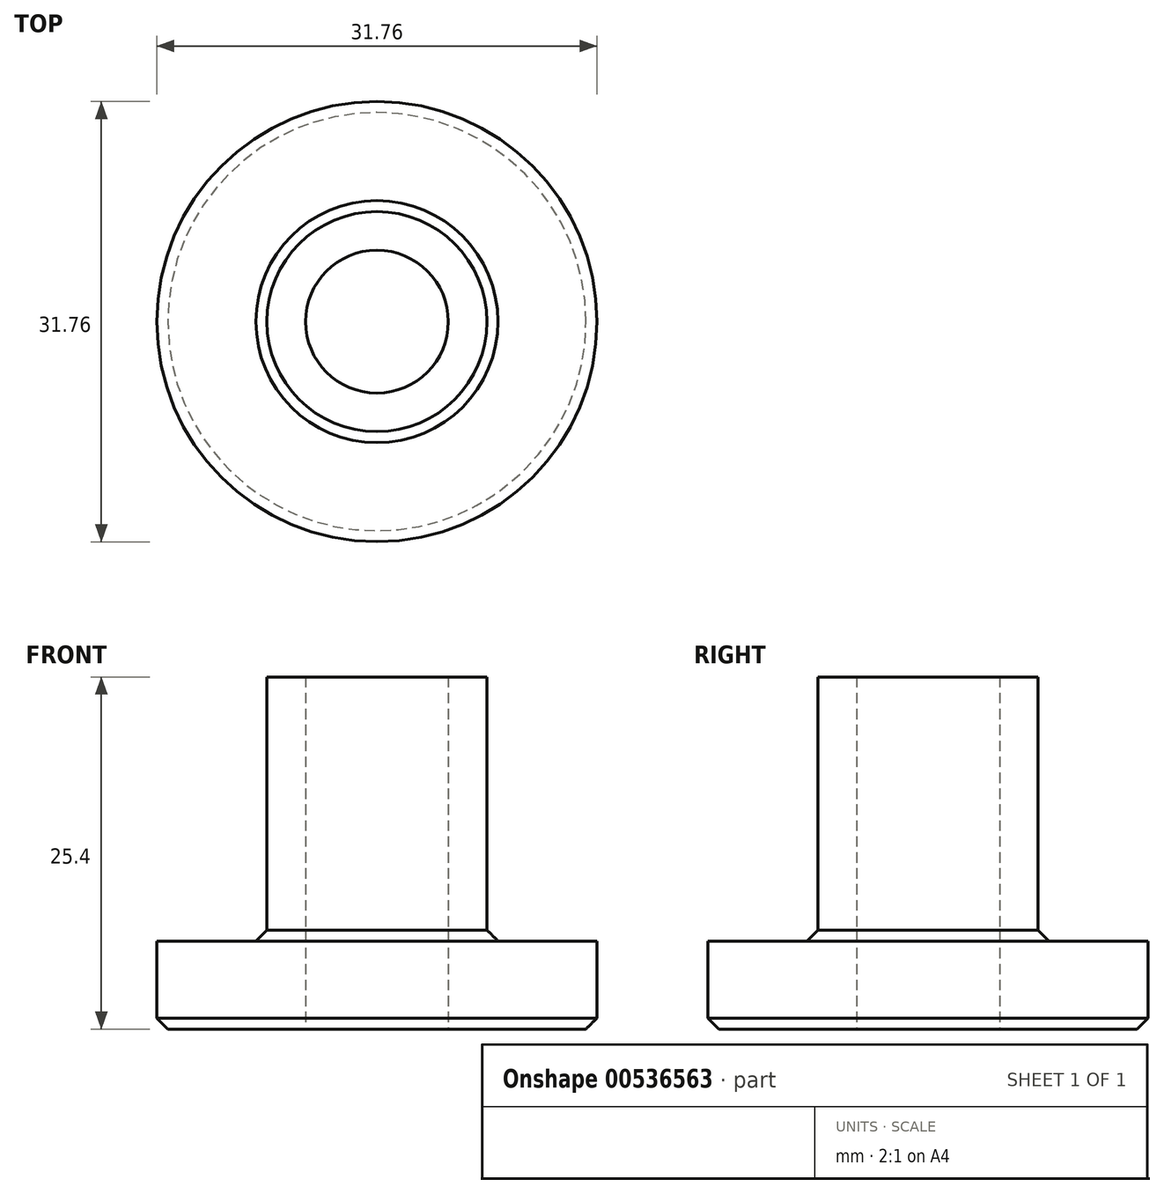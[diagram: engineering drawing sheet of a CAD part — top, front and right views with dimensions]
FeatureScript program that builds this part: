
annotation { "Feature Type Name" : "Feature", "Feature Type Description" : "" }
export const myFeature = defineFeature(function(context is Context, id is Id, definition is map)
    precondition{}
    {
        {
            var Q0;
            Q0=qCreatedBy(makeId("Top.planeOp"),FACE);
            var sketch = newSketch(context, id + "F0", { "sketchPlane" : qUnion([Q0])});
            skCircle(sketch, "E0", {"center": v(0, 0) * mm, "radius": 15.88 * mm});
            skSolve(sketch);
        }
        {
            var Q0;
            Q0=qSketchRegion(id+"F0",true);
            extrude(context, id + "F1", {"entities" : qUnion([Q0]), "depth" : 25.4 * mm, "offsetDistance" : 25.4 * mm});
        }
        {
            var Q0;
            Q0=sQuery(id+"F0.wireOp",VERTEX,"E0.center");
            var Q1;
            Q1=makeQuery(id+"F1.opExtrude","SWEPT_BODY",BODY,{"disambiguationData":[OSD([sQuery(id+"F0.wireOp",EDGE,"E0")])]});
            hole(context, id + "F2", {"style" : HoleStyle.SIMPLE, "endStyle" : HoleEndStyle.THROUGH, "oppositeDirection" : true, "standardTappedOrClearance" : lookupTablePath({ "standard" : "ISO", "engagement" : "75%", "pitch" : "1.75 mm", "size" : "M12", "type" : "Tapped" }), "standardBlindInLast" : lookupTablePath({ "standard" : "ISO", "engagement" : "75%", "pitch" : "1.75 mm", "size" : "M12", "type" : "Tapped" }), "holeDiameter" : 10.3 * mm, "showTappedDepth" : true, "isTappedThrough" : true, "tappedDepth" : 15.88 * mm, "tapClearance" : 3, "startFromSketch" : true, "locations" : qUnion([Q0]), "scope" : qUnion([Q1]), "majorDiameter" : 12 * mm});
        }
        {
            var Q0;
            Q0=makeQuery(id+"F1.opExtrude","CAP_EDGE",EDGE,{"disambiguationData":[OSD([sQuery(id+"F0.wireOp",EDGE,"E0")])],"isStart":true});
            chamfer(context, id + "F3", {"entities" : qUnion([Q0]), "width" : 0.8 * mm, "tangentPropagation" : true});
        }
        {
            var Q0;
            Q0=makeQuery(id+"F1.opExtrude","CAP_EDGE",EDGE,{"disambiguationData":[OSD([sQuery(id+"F0.wireOp",EDGE,"E0")])],"isStart":false});
            var Q1;
            Q1=makeQuery(id+"F2.hole-0.boolean.opBoolean","COPY",EDGE,{"derivedFrom":makeQuery(id+"F2.hole-0.opRevolve","SWEPT_EDGE",EDGE,{"disambiguationData":[OSD([sQuery(id+"F2.hole-0.sketch.wireOp",EDGE,"core_line_2"),sQuery(id+"F2.hole-0.sketch.wireOp",EDGE,"core_line_3")])]})});
            var Q2;
            Q2=makeQuery(id+"F2.hole-0.boolean.opBoolean","INTERSECT",EDGE,{"derivedFrom":[makeQuery(id+"F1.opExtrude","CAP_FACE",FACE,{"disambiguationData":[OSD([sQuery(id+"F0.wireOp",EDGE,"E0")])],"isStart":false}),makeQuery(id+"F2.hole-0.opRevolve","SWEPT_FACE",FACE,{"disambiguationData":[OSD([sQuery(id+"F2.hole-0.sketch.wireOp",EDGE,"core_line_2")])]})]});
            chamfer(context, id + "F4", {"entities" : qUnion([Q0, Q1, Q2]), "width" : 0.8 * mm, "tangentPropagation" : true});
        }
        {
            var Q0;
            Q0=makeQuery(id+"F1.opExtrude","CAP_FACE",FACE,{"disambiguationData":[OSD([sQuery(id+"F0.wireOp",EDGE,"E0")])],"isStart":false});
            var sketch = newSketch(context, id + "F5", { "sketchPlane" : qUnion([Q0])});
            skCircle(sketch, "E1", {"center": v(0, 0) * mm, "radius": 7.94 * mm});
            skCircle(sketch, "E2", {"center": v(0, 0) * mm, "radius": 15.88 * mm});
            skSolve(sketch);
        }
        {
            var Q0;
            Q0=qSketchRegion(id+"F5",true);
            extrude(context, id + "F6", {"entities" : qUnion([Q0]), "operationType" : NewBodyOperationType.REMOVE, "oppositeDirection" : true, "depth" : 19.05 * mm, "offsetDistance" : 25.4 * mm});
        }
        {
            var Q0;
            Q0=makeQuery(id+"F6.boolean.opBoolean","COPY",EDGE,{"derivedFrom":makeQuery(id+"F6.opExtrude","CAP_EDGE",EDGE,{"disambiguationData":[OSD([sQuery(id+"F5.wireOp",EDGE,"E2")])],"isStart":false})});
            var Q1;
            Q1=makeQuery(id+"F6.boolean.opBoolean","COPY",EDGE,{"derivedFrom":makeQuery(id+"F6.opExtrude","CAP_EDGE",EDGE,{"disambiguationData":[OSD([sQuery(id+"F5.wireOp",EDGE,"E1")])],"isStart":false})});
            var Q2;
            Q2=makeQuery(id+"F6.boolean.opBoolean","COPY",EDGE,{"derivedFrom":makeQuery(id+"F6.opExtrude","CAP_EDGE",EDGE,{"disambiguationData":[OSD([sQuery(id+"F5.wireOp",EDGE,"E1")])],"isStart":true})});
            chamfer(context, id + "F7", {"entities" : qUnion([Q0, Q1, Q2]), "width" : 0.8 * mm, "tangentPropagation" : true});
        }
    });
